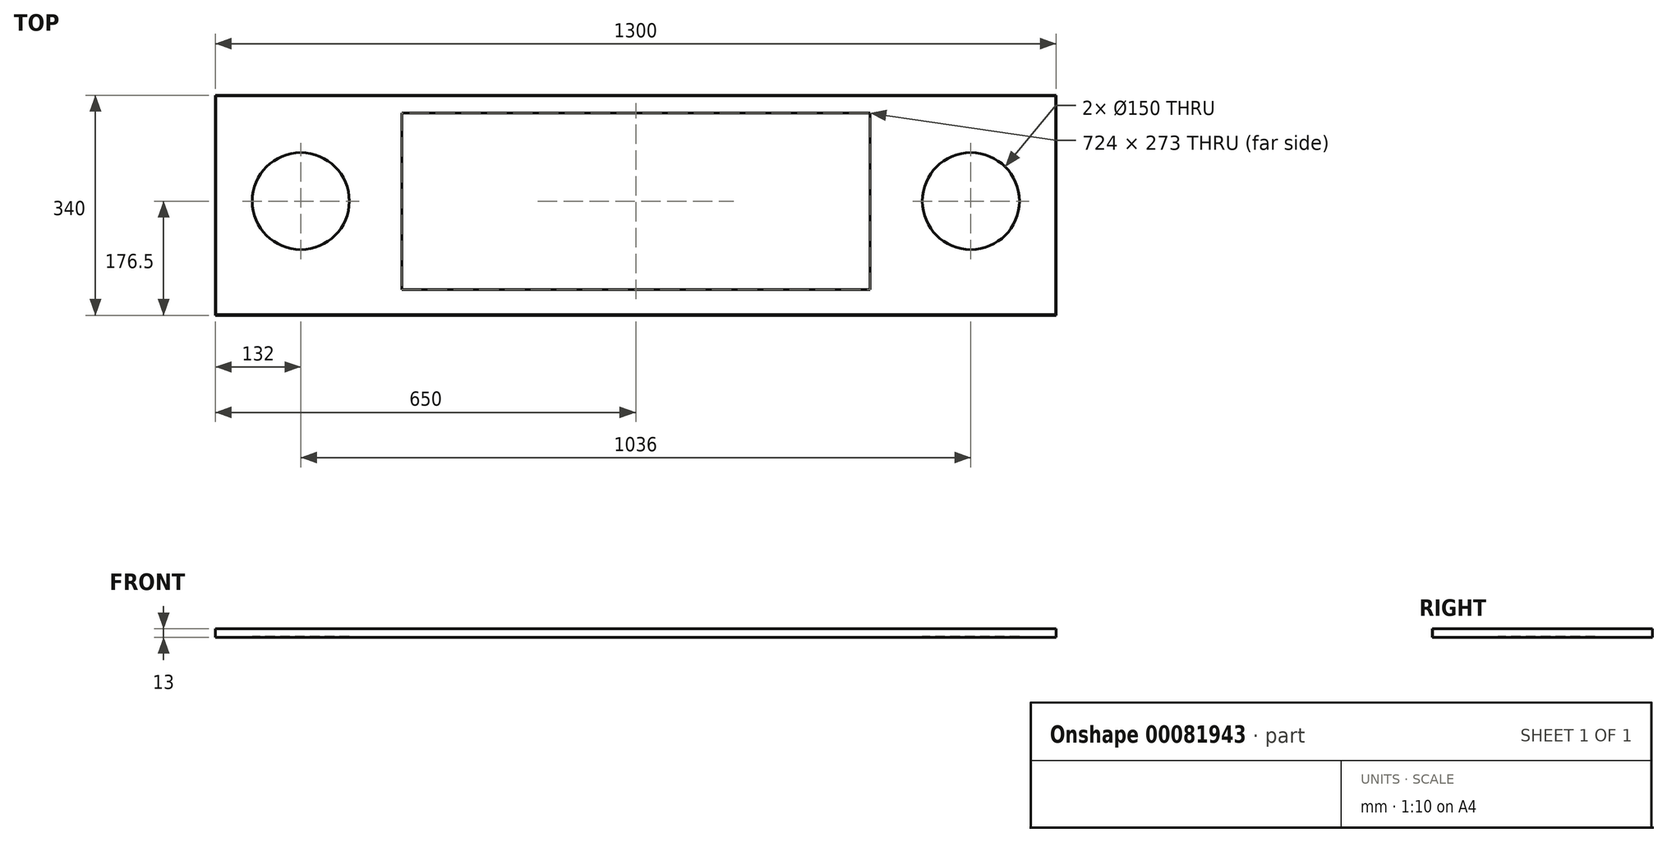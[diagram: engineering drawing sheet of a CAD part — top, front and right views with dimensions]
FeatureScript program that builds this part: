
annotation { "Feature Type Name" : "Feature", "Feature Type Description" : "" }
export const myFeature = defineFeature(function(context is Context, id is Id, definition is map)
    precondition{}
    {
        {
            var Q0;
            Q0=qCreatedBy(makeId("Top.planeOp"),FACE);
            var sketch = newSketch(context, id + "F0", { "sketchPlane" : qUnion([Q0])});
            skLineSegment(sketch, "E0.bottom", {"start": v(-650, -170) * mm, "end": v(650, -170) * mm});
            skLineSegment(sketch, "E0.top", {"start": v(-650, 170) * mm, "end": v(650, 170) * mm});
            skLineSegment(sketch, "E0.left", {"start": v(-650, -170) * mm, "end": v(-650, 170) * mm});
            skLineSegment(sketch, "E0.right", {"start": v(650, -170) * mm, "end": v(650, 170) * mm});
            skPoint(sketch, "E0.middle", {"position": v(0, 0) * mm});
            skSolve(sketch);
        }
        {
            var Q0;
            Q0=makeQuery(id+"F0.imprint","IMPRINT",FACE,{"disambiguationData":[TD([[makeQuery(id+"F0.imprint","IMPRINT",EDGE,{"derivedFrom":sQuery(id+"F0.wireOp",EDGE,"E0.bottom")}),1.0]])]});
            var Q1;
            Q1=sQuery(id+"F0.wireOp",EDGE,"E0.top");
            var Q2;
            Q2=sQuery(id+"F0.wireOp",EDGE,"E0.left");
            var Q3;
            Q3=sQuery(id+"F0.wireOp",EDGE,"E0.right");
            var Q4;
            Q4=sQuery(id+"F0.wireOp",EDGE,"E0.bottom");
            extrude(context, id + "F1", {"entities" : qUnion([Q0]), "surfaceEntities" : qUnion([Q1, Q2, Q3, Q4]), "depth" : 13 * mm});
        }
        {
            var Q0;
            Q0=makeQuery(id+"F1.opExtrude","CAP_FACE",FACE,{"disambiguationData":[OSD([sQuery(id+"F0.wireOp",EDGE,"E0.bottom"),sQuery(id+"F0.wireOp",EDGE,"E0.top"),sQuery(id+"F0.wireOp",EDGE,"E0.left"),sQuery(id+"F0.wireOp",EDGE,"E0.right")])],"isStart":false});
            shell(context, id + "F2", {"entities" : qUnion([Q0]), "thickness" : 0.9 * mm});
        }
        {
            var Q0;
            Q0=makeQuery(id+"F2.opShell","OFFSET_FACE",FACE,{"disambiguationData":[OSD([sQuery(id+"F0.wireOp",EDGE,"E0.bottom"),sQuery(id+"F0.wireOp",EDGE,"E0.top"),sQuery(id+"F0.wireOp",EDGE,"E0.left"),sQuery(id+"F0.wireOp",EDGE,"E0.right")])]});
            var sketch = newSketch(context, id + "F3", { "sketchPlane" : qUnion([Q0])});
            skLineSegment(sketch, "E1", {"start": v(0, 169.1) * mm, "end": v(0, -169.1) * mm, "construction": true});
            skLineSegment(sketch, "E2.bottom", {"start": v(-362, -130) * mm, "end": v(362, -130) * mm});
            skLineSegment(sketch, "E2.top", {"start": v(-362, 143) * mm, "end": v(362, 143) * mm});
            skLineSegment(sketch, "E2.left", {"start": v(-362, -130) * mm, "end": v(-362, 143) * mm});
            skLineSegment(sketch, "E2.right", {"start": v(362, -130) * mm, "end": v(362, 143) * mm});
            skSolve(sketch);
        }
        {
            var Q0;
            Q0 = qSketchRegion(id + "F3", true);
            extrude(context, id + "F4", {"entities" : qUnion([Q0]), "operationType" : NewBodyOperationType.REMOVE, "endBound" : BoundingType.THROUGH_ALL, "oppositeDirection" : true, "depth" : 25 * mm, "hasSecondDirection" : true, "secondDirectionBound" : SecondDirectionBoundingType.THROUGH_ALL, "secondDirectionOppositeDirection" : false, "secondDirectionDepth" : 25 * mm});
        }
        {
            var Q0;
            Q0=makeQuery(id+"F2.opShell","OFFSET_FACE",FACE,{"disambiguationData":[OSD([sQuery(id+"F0.wireOp",EDGE,"E0.bottom"),sQuery(id+"F0.wireOp",EDGE,"E0.top"),sQuery(id+"F0.wireOp",EDGE,"E0.left"),sQuery(id+"F0.wireOp",EDGE,"E0.right")])]});
            var sketch = newSketch(context, id + "F5", { "sketchPlane" : qUnion([Q0])});
            skLineSegment(sketch, "E3", {"start": v(-362, 6.5) * mm, "end": v(-763.78, 6.5) * mm, "construction": true});
            skCircle(sketch, "E4", {"center": v(-518, 6.5) * mm, "radius": 75 * mm});
            skCircle(sketch, "E5.MirrorC", {"center": v(518, 6.5) * mm, "radius": 75 * mm});
            skSolve(sketch);
        }
        {
            var Q0;
            Q0 = qSketchRegion(id + "F5", true);
            extrude(context, id + "F6", {"entities" : qUnion([Q0]), "operationType" : NewBodyOperationType.REMOVE, "endBound" : BoundingType.THROUGH_ALL, "depth" : 25 * mm, "hasSecondDirection" : true, "secondDirectionBound" : SecondDirectionBoundingType.THROUGH_ALL, "secondDirectionOppositeDirection" : true, "secondDirectionDepth" : 25 * mm});
        }
    });
